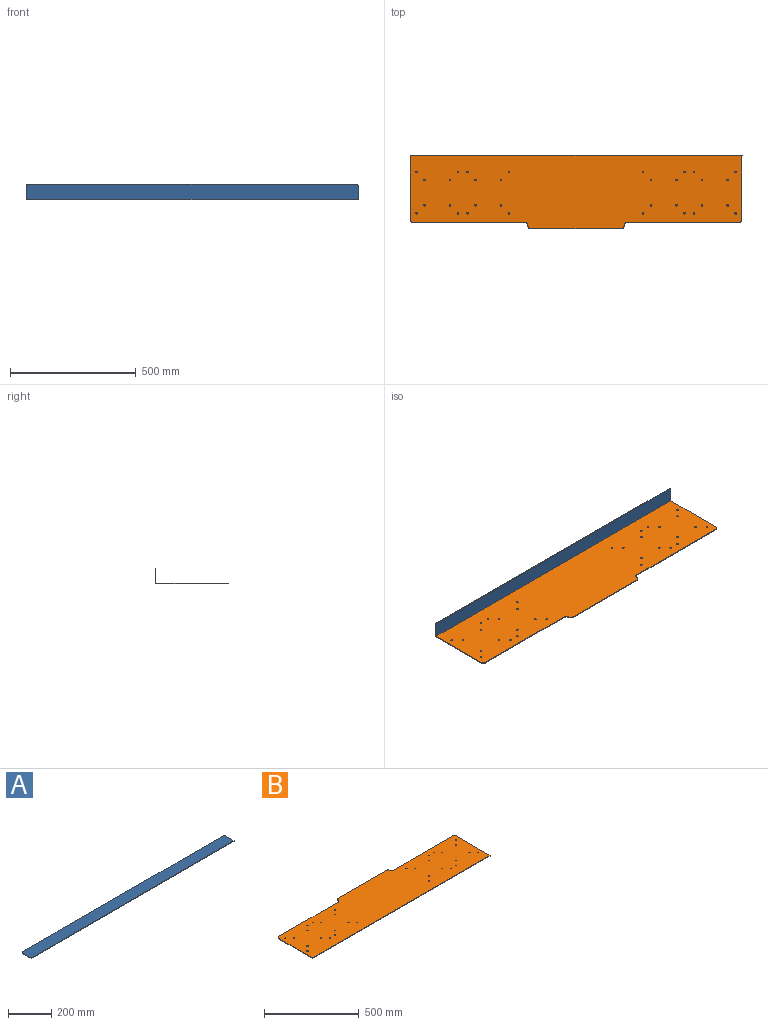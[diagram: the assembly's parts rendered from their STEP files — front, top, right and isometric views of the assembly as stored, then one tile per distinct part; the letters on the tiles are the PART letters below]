
ASSEMBLY  parts=2 mates=1
PART A: 8 faces, bbox 1320.8x63.5x3.2 mm
  f0: plane 1308.1x3.18mm, normal (0,1,0), area 4153.2mm2, adj f4,f5,f6,f7
  f1: plane 57.15x3.18mm, normal (-1,0,0), area 181.5mm2, adj f2,f4,f5,f6
  f2: plane 1320.8x3.18mm, normal (0,-1,0), area 4193.5mm2, adj f1,f3,f4,f5
  f3: plane 57.15x3.18mm, normal (1,0,0), area 181.5mm2, adj f2,f4,f5,f7
  f4: plane 1320.8x63.5mm, normal (0,0,1), area 83853.5mm2, adj f0,f1,f2,f3,f6,f7
  f5: plane 1320.8x63.5mm, normal (0,0,-1), area 83853.5mm2, adj f0,f1,f2,f3,f6,f7
  f6: cylinder r=6.35mm len=6.35mm, axis (0,0,1), area 31.7mm2, adj f0,f1,f4,f5
  f7: cylinder r=6.35mm len=6.35mm, axis (0,0,-1), area 31.7mm2, adj f0,f3,f4,f5
PART B: 46 faces, bbox 1320.8x290.8x3.2 mm
  f0: plane 252.73x3.18mm, normal (-1,0,0), area 802.4mm2, adj f2,f3,f4,f40
  f1: plane 252.73x3.18mm, normal (1,0,0), area 802.4mm2, adj f2,f3,f4,f45
  f2: plane 1320.8x290.83mm, normal (0,0,1), area 359239.2mm2, adj f0,f1,f4,f5,f6,f7,f8,f9
  f3: plane 1320.8x290.83mm, normal (0,0,-1), area 359239.2mm2, adj f0,f1,f4,f5,f6,f7,f8,f9
  f4: plane 1320.8x3.18mm, normal (0,-1,0), area 4193.5mm2, adj f0,f1,f2,f3
  f5: cylinder r=3.17mm len=6.35mm, axis (0,0,1), area 63.3mm2, adj f2,f3
  f6: cylinder r=3.17mm len=6.35mm, axis (0,0,1), area 63.3mm2, adj f2,f3
  f7: cylinder r=3.17mm len=6.35mm, axis (0,0,1), area 63.3mm2, adj f2,f3
  f8: cylinder r=3.17mm len=6.35mm, axis (0,0,1), area 63.3mm2, adj f2,f3
  f9: cylinder r=3.17mm len=6.35mm, axis (0,0,1), area 63.3mm2, adj f2,f3
  f10: cylinder r=3.17mm len=6.35mm, axis (0,0,1), area 63.3mm2, adj f2,f3
  f11: cylinder r=3.17mm len=6.35mm, axis (0,0,1), area 63.3mm2, adj f2,f3
  f12: cylinder r=3.17mm len=6.35mm, axis (0,0,1), area 63.3mm2, adj f2,f3
  f13: cylinder r=3.17mm len=6.35mm, axis (0,0,1), area 63.3mm2, adj f2,f3
  f14: cylinder r=3.17mm len=6.35mm, axis (0,0,1), area 63.3mm2, adj f2,f3
  f15: cylinder r=3.17mm len=6.35mm, axis (0,0,1), area 63.3mm2, adj f2,f3
  f16: cylinder r=3.17mm len=6.35mm, axis (0,0,1), area 63.3mm2, adj f2,f3
  f17: cylinder r=3.17mm len=6.35mm, axis (0,0,1), area 63.3mm2, adj f2,f3
  f18: cylinder r=3.17mm len=6.35mm, axis (0,0,1), area 63.3mm2, adj f2,f3
  f19: cylinder r=3.17mm len=6.35mm, axis (0,0,1), area 63.3mm2, adj f2,f3
  f20: cylinder r=3.17mm len=6.35mm, axis (0,0,1), area 63.3mm2, adj f2,f3
  f21: cylinder r=3.17mm len=6.35mm, axis (0,0,1), area 63.3mm2, adj f2,f3
  f22: cylinder r=3.17mm len=6.35mm, axis (0,0,1), area 63.3mm2, adj f2,f3
  f23: cylinder r=3.17mm len=6.35mm, axis (0,0,1), area 63.3mm2, adj f2,f3
  f24: cylinder r=3.17mm len=6.35mm, axis (0,0,1), area 63.3mm2, adj f2,f3
  f25: cylinder r=3.17mm len=6.35mm, axis (0,0,1), area 63.3mm2, adj f2,f3
  f26: cylinder r=3.17mm len=6.35mm, axis (0,0,1), area 63.3mm2, adj f2,f3
  f27: cylinder r=3.17mm len=6.35mm, axis (0,0,1), area 63.3mm2, adj f2,f3
  f28: cylinder r=3.17mm len=6.35mm, axis (0,0,1), area 63.3mm2, adj f2,f3
  f29: cylinder r=3.17mm len=6.35mm, axis (0,0,1), area 63.3mm2, adj f2,f3
  f30: cylinder r=3.17mm len=6.35mm, axis (0,0,1), area 63.3mm2, adj f2,f3
  f31: cylinder r=3.17mm len=6.35mm, axis (0,0,1), area 63.3mm2, adj f2,f3
  f32: cylinder r=3.17mm len=6.35mm, axis (0,0,1), area 63.3mm2, adj f2,f3
  f33: cylinder r=3.17mm len=6.35mm, axis (0,0,1), area 63.3mm2, adj f2,f3
  f34: cylinder r=3.17mm len=6.35mm, axis (0,0,1), area 63.3mm2, adj f2,f3
  f35: cylinder r=3.17mm len=6.35mm, axis (0,0,1), area 63.3mm2, adj f2,f3
  f36: cylinder r=3.17mm len=6.35mm, axis (0,0,1), area 63.3mm2, adj f2,f3
  f37: plane 358.14x3.18mm, normal (0,1,0), area 1137.1mm2, adj f2,f3,f41,f44
  f38: plane 443.23x3.18mm, normal (0,1,0), area 1407.3mm2, adj f2,f3,f43,f45
  f39: plane 443.23x3.18mm, normal (0,1,0), area 1407.3mm2, adj f2,f3,f40,f42
  f40: cylinder r=12.7mm len=12.7mm, axis (0,0,1), area 63.3mm2, adj f0,f2,f3,f39
  f41: cylinder r=12.7mm len=12.7mm, axis (0,0,-1), area 63.3mm2, adj f2,f3,f37,f42
  f42: cylinder r=12.7mm len=12.7mm, axis (0,0,1), area 63.3mm2, adj f2,f3,f39,f41
  f43: cylinder r=12.7mm len=12.7mm, axis (0,0,1), area 63.3mm2, adj f2,f3,f38,f44
  f44: cylinder r=12.7mm len=12.7mm, axis (0,0,1), area 63.3mm2, adj f2,f3,f37,f43
  f45: cylinder r=12.7mm len=12.7mm, axis (0,0,1), area 63.3mm2, adj f1,f2,f3,f38
PLACE A rot(axis=(0,0.71,0.71),180deg) t=(0,136.59,31.69)mm
PLACE B rot(axis=(1,0,0),180deg) t=(0,-18.98,3.18)mm
MATE fastened B.f4 <-> A.f5  axis (0,1,0) through (0,136.59,1.59)mm
